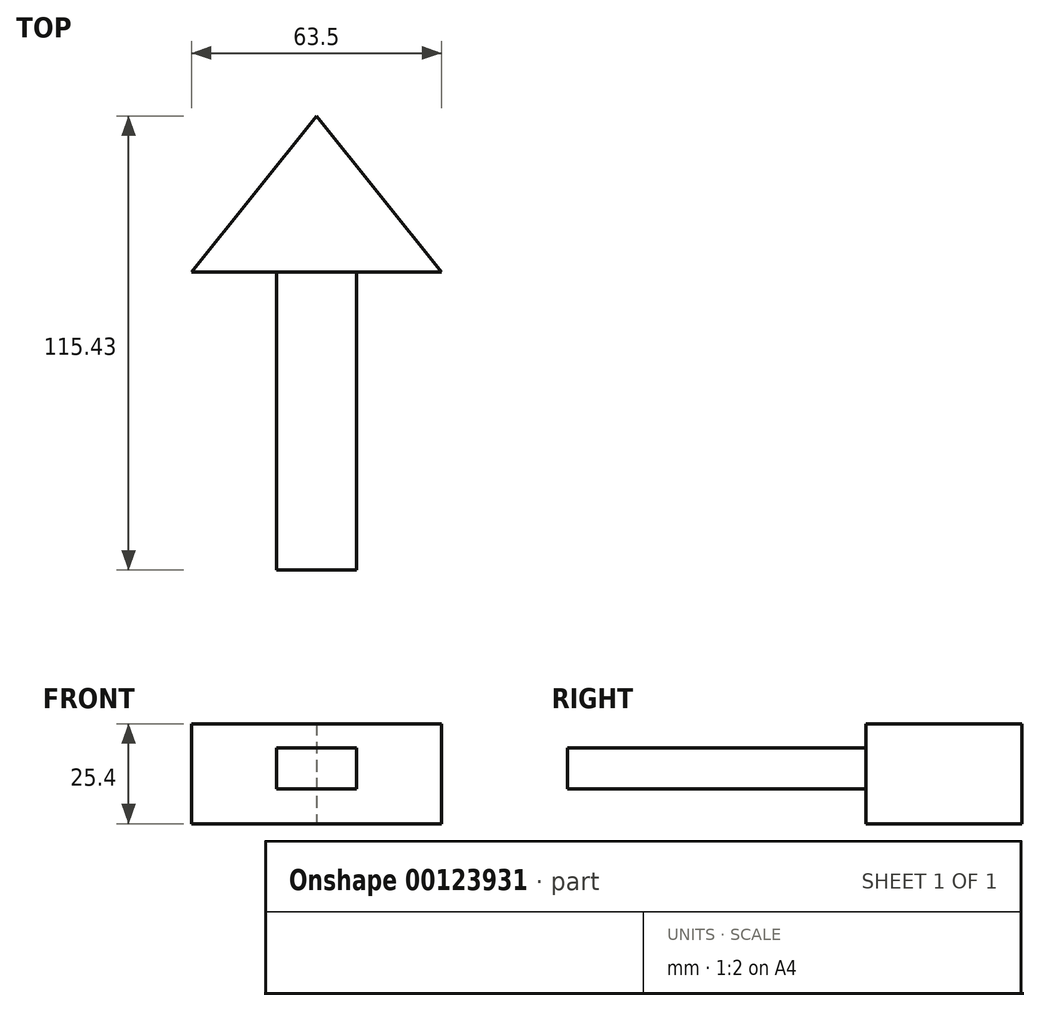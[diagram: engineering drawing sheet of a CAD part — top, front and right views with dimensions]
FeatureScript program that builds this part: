
annotation { "Feature Type Name" : "Feature", "Feature Type Description" : "" }
export const myFeature = defineFeature(function(context is Context, id is Id, definition is map)
    precondition{}
    {
        {
            var Q0;
            Q0=qCreatedBy(makeId("Top.planeOp"),FACE);
            var sketch = newSketch(context, id + "F0", { "sketchPlane" : qUnion([Q0])});
            skLineSegment(sketch, "E0", {"start": v(0, 39.66) * mm, "end": v(-31.75, 0) * mm});
            skLineSegment(sketch, "E1", {"start": v(-31.75, 0) * mm, "end": v(31.75, 0) * mm});
            skLineSegment(sketch, "E2", {"start": v(31.75, 0) * mm, "end": v(0, 39.66) * mm});
            skSolve(sketch);
        }
        {
            var Q0;
            Q0=makeQuery(id+"F0.imprint","IMPRINT",FACE,{"disambiguationData":[TD([[makeQuery(id+"F0.imprint","IMPRINT",EDGE,{"derivedFrom":sQuery(id+"F0.wireOp",EDGE,"E0")}),1.0]])]});
            extrude(context, id + "F1", {"entities" : qUnion([Q0]), "depth" : 25.4 * mm});
        }
        {
            var Q0;
            Q0=qCreatedBy(makeId("Right.planeOp"),FACE);
            var sketch = newSketch(context, id + "F2", { "sketchPlane" : qUnion([Q0])});
            skLineSegment(sketch, "E3", {"start": v(0, 19.2) * mm, "end": v(0, 8.9) * mm});
            skLineSegment(sketch, "E4", {"start": v(0, 8.9) * mm, "end": v(-75.77, 8.9) * mm});
            skLineSegment(sketch, "E5", {"start": v(-75.77, 8.9) * mm, "end": v(-75.77, 19.2) * mm});
            skLineSegment(sketch, "E6", {"start": v(-75.77, 19.2) * mm, "end": v(0, 19.2) * mm});
            skLineSegment(sketch, "E7", {"start": v(0, 8.9) * mm, "end": v(0, 19.2) * mm});
            skSolve(sketch);
        }
        {
            var Q0;
            Q0 = qSketchRegion(id + "F2", true);
            extrude(context, id + "F3", {"entities" : qUnion([Q0]), "operationType" : NewBodyOperationType.ADD, "endBound" : BoundingType.SYMMETRIC, "depth" : 20.26 * mm});
        }
    });
